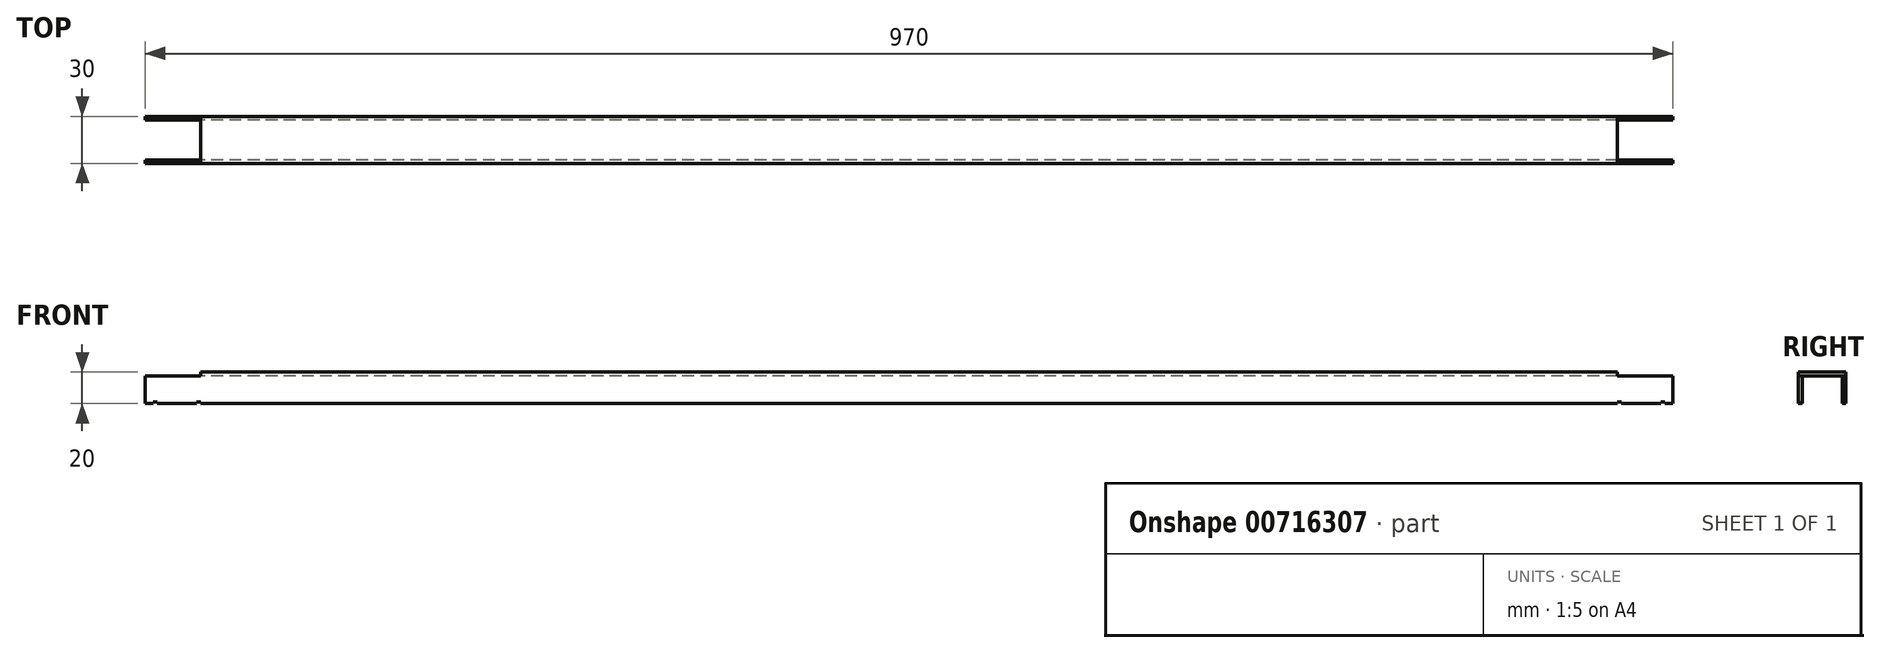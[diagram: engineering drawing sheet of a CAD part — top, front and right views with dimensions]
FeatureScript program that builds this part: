
annotation { "Feature Type Name" : "Feature", "Feature Type Description" : "" }
export const myFeature = defineFeature(function(context is Context, id is Id, definition is map)
    precondition{}
    {
        {
            var Q0;
            Q0=qCreatedBy(makeId("Right.planeOp"),FACE);
            var sketch = newSketch(context, id + "F0", { "sketchPlane" : qUnion([Q0])});
            skLineSegment(sketch, "E0.bottom", {"start": v(0, 0) * mm, "end": v(2.3, 0) * mm});
            skLineSegment(sketch, "E0.top", {"start": v(0, 20) * mm, "end": v(30, 20) * mm});
            skLineSegment(sketch, "E0.left", {"start": v(0, 0) * mm, "end": v(0, 20) * mm});
            skLineSegment(sketch, "E0.right", {"start": v(30, 0) * mm, "end": v(30, 20) * mm});
            skLineSegment(sketch, "E1.0", {"start": v(27.7, 0) * mm, "end": v(27.7, 17.7) * mm});
            skLineSegment(sketch, "E2.0", {"start": v(2.3, 17.7) * mm, "end": v(27.7, 17.7) * mm});
            skLineSegment(sketch, "E3.0", {"start": v(2.3, 0) * mm, "end": v(2.3, 17.7) * mm});
            skLineSegment(sketch, "E4.trimOffspring", {"start": v(27.7, 0) * mm, "end": v(30, 0) * mm});
            skSolve(sketch);
        }
        {
            var Q0;
            Q0=qSketchRegion(id+"F0",true);
            extrude(context, id + "F1", {"entities" : qUnion([Q0]), "depth" : 970 * mm, "offsetDistance" : 25 * mm});
        }
        {
            var Q0;
            Q0=makeQuery(id+"F1.opExtrude","SWEPT_FACE",FACE,{"disambiguationData":[OSD([sQuery(id+"F0.wireOp",EDGE,"E0.top")])]});
            var sketch = newSketch(context, id + "F2", { "sketchPlane" : qUnion([Q0])});
            skLineSegment(sketch, "E5.bottom", {"start": v(0, 0) * mm, "end": v(35, 0) * mm});
            skLineSegment(sketch, "E5.top", {"start": v(0, 30) * mm, "end": v(35, 30) * mm});
            skLineSegment(sketch, "E5.left", {"start": v(0, 0) * mm, "end": v(0, 30) * mm});
            skLineSegment(sketch, "E5.right", {"start": v(35, 0) * mm, "end": v(35, 30) * mm});
            skLineSegment(sketch, "E6.bottom", {"start": v(970, 0) * mm, "end": v(935, 0) * mm});
            skLineSegment(sketch, "E6.top", {"start": v(970, 30) * mm, "end": v(935, 30) * mm});
            skLineSegment(sketch, "E6.left", {"start": v(970, 0) * mm, "end": v(970, 30) * mm});
            skLineSegment(sketch, "E6.right", {"start": v(935, 0) * mm, "end": v(935, 30) * mm});
            skSolve(sketch);
        }
        {
            var Q0;
            Q0=qSketchRegion(id+"F2",true);
            extrude(context, id + "F3", {"entities" : qUnion([Q0]), "operationType" : NewBodyOperationType.REMOVE, "oppositeDirection" : true, "depth" : 2.3 * mm, "offsetDistance" : 25 * mm});
        }
        {
            var Q0;
            Q0=makeQuery(id+"F1.opExtrude","SWEPT_FACE",FACE,{"disambiguationData":[OSD([sQuery(id+"F0.wireOp",EDGE,"E0.left")])]});
            var sketch = newSketch(context, id + "F4", { "sketchPlane" : qUnion([Q0])});
            skLineSegment(sketch, "E7.bottom", {"start": v(35, 0) * mm, "end": v(32.6, 0) * mm});
            skLineSegment(sketch, "E7.top", {"start": v(35, 1) * mm, "end": v(32.6, 1) * mm});
            skLineSegment(sketch, "E7.left", {"start": v(35, 0) * mm, "end": v(35, 1) * mm});
            skLineSegment(sketch, "E7.right", {"start": v(32.6, 0) * mm, "end": v(32.6, 1) * mm});
            skLineSegment(sketch, "E8.bottom", {"start": v(7.4, 0) * mm, "end": v(5, 0) * mm});
            skLineSegment(sketch, "E8.top", {"start": v(7.4, 1) * mm, "end": v(5, 1) * mm});
            skLineSegment(sketch, "E8.left", {"start": v(7.4, 0) * mm, "end": v(7.4, 1) * mm});
            skLineSegment(sketch, "E8.right", {"start": v(5, 0) * mm, "end": v(5, 1) * mm});
            skLineSegment(sketch, "E9", {"start": v(485, 128) * mm, "end": v(485, 0) * mm, "construction": true});
            skLineSegment(sketch, "E10.MirrorCS", {"start": v(937.4, 0) * mm, "end": v(937.4, 1) * mm});
            skLineSegment(sketch, "E11.MirrorCS", {"start": v(935, 1) * mm, "end": v(937.4, 1) * mm});
            skLineSegment(sketch, "E12.MirrorCS", {"start": v(935, 0) * mm, "end": v(935, 1) * mm});
            skLineSegment(sketch, "E13.MirrorCS", {"start": v(965, 0) * mm, "end": v(965, 1) * mm});
            skLineSegment(sketch, "E14.MirrorCS", {"start": v(962.6, 1) * mm, "end": v(965, 1) * mm});
            skLineSegment(sketch, "E15.MirrorCS", {"start": v(962.6, 0) * mm, "end": v(962.6, 1) * mm});
            skLineSegment(sketch, "E16.MirrorCS", {"start": v(962.6, 0) * mm, "end": v(965, 0) * mm});
            skLineSegment(sketch, "E17.MirrorCS", {"start": v(935, 0) * mm, "end": v(937.4, 0) * mm});
            skSolve(sketch);
        }
        {
            var Q0;
            Q0=qSketchRegion(id+"F4",true);
            extrude(context, id + "F5", {"entities" : qUnion([Q0]), "operationType" : NewBodyOperationType.REMOVE, "endBound" : BoundingType.THROUGH_ALL, "oppositeDirection" : true, "depth" : 25 * mm, "offsetDistance" : 25 * mm});
        }
    });
